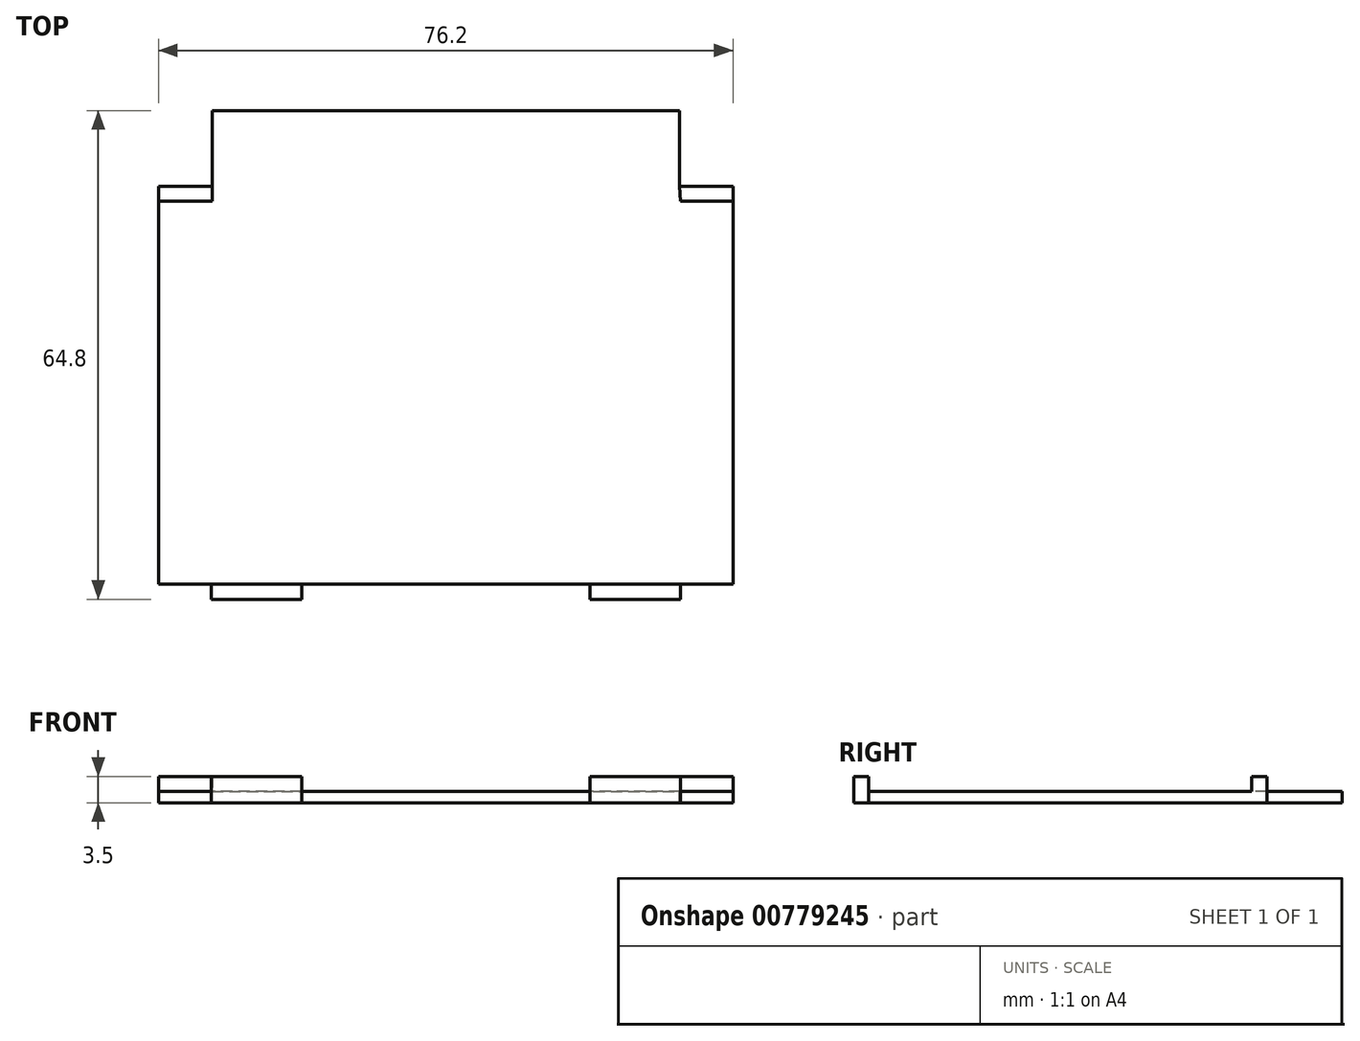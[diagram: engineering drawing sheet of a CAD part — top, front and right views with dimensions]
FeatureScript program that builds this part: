
annotation { "Feature Type Name" : "Feature", "Feature Type Description" : "" }
export const myFeature = defineFeature(function(context is Context, id is Id, definition is map)
    precondition{}
    {
        {
            var Q0;
            Q0=qCreatedBy(makeId("Top.planeOp"),FACE);
            var sketch = newSketch(context, id + "F0", { "sketchPlane" : qUnion([Q0])});
            skLineSegment(sketch, "E0.bottom", {"start": v(38.1, -25.4) * mm, "end": v(-38.1, -25.4) * mm});
            skLineSegment(sketch, "E0.top", {"start": v(38.1, 25.4) * mm, "end": v(-38.1, 25.4) * mm});
            skLineSegment(sketch, "E0.left", {"start": v(38.1, -25.4) * mm, "end": v(38.1, 25.4) * mm});
            skLineSegment(sketch, "E0.right", {"start": v(-38.1, -25.4) * mm, "end": v(-38.1, 25.4) * mm});
            skPoint(sketch, "E0.middle", {"position": v(0, 0) * mm});
            skLineSegment(sketch, "E1", {"start": v(-36.6, 25.4) * mm, "end": v(-36.6, -25.4) * mm});
            skLineSegment(sketch, "E2", {"start": v(-38.1, 25.4) * mm, "end": v(-38.1, 27.4) * mm});
            skLineSegment(sketch, "E3", {"start": v(-38.1, 27.4) * mm, "end": v(-31, 27.4) * mm});
            skLineSegment(sketch, "E4", {"start": v(-31.1, -25.4) * mm, "end": v(-31.1, -27.4) * mm});
            skLineSegment(sketch, "E5", {"start": v(-31.1, -27.4) * mm, "end": v(-19.1, -27.4) * mm});
            skLineSegment(sketch, "E6", {"start": v(-19.1, -27.4) * mm, "end": v(-19.1, -25.4) * mm});
            skLineSegment(sketch, "E7", {"start": v(0, 25.4) * mm, "end": v(0, -25.4) * mm, "construction": true});
            skLineSegment(sketch, "E8.MirrorCS", {"start": v(19.1, -27.4) * mm, "end": v(19.1, -25.4) * mm});
            skLineSegment(sketch, "E9.MirrorCS", {"start": v(31.1, -27.4) * mm, "end": v(19.1, -27.4) * mm});
            skLineSegment(sketch, "E10.MirrorCS", {"start": v(31.1, -25.4) * mm, "end": v(31.1, -27.4) * mm});
            skLineSegment(sketch, "E11.MirrorCS", {"start": v(36.6, 25.4) * mm, "end": v(36.6, -25.4) * mm});
            skLineSegment(sketch, "E12.MirrorCS", {"start": v(38.1, 25.4) * mm, "end": v(38.1, 27.4) * mm});
            skLineSegment(sketch, "E13.MirrorCS", {"start": v(38.1, 27.4) * mm, "end": v(31, 27.4) * mm});
            skLineSegment(sketch, "E14.MirrorCS", {"start": v(31, 27.4) * mm, "end": v(31.1, 25.4) * mm});
            skLineSegment(sketch, "E15.bottom", {"start": v(-31, 37.4) * mm, "end": v(31, 37.4) * mm});
            skLineSegment(sketch, "E15.left", {"start": v(-31, 37.4) * mm, "end": v(-31, 25.4) * mm});
            skLineSegment(sketch, "E15.right", {"start": v(31, 37.4) * mm, "end": v(31, 25.4) * mm});
            skLineSegment(sketch, "E16", {"start": v(0, 25.4) * mm, "end": v(0, 37.4) * mm});
            skSolve(sketch);
        }
        {
            var Q0;
            Q0 = qSketchRegion(id + "F0", true);
            extrude(context, id + "F1", {"entities" : qUnion([Q0]), "oppositeDirection" : true, "depth" : 1.5 * mm, "offsetDistance" : 25 * mm});
        }
        {
            var Q0;
            {var subQ1=sQuery(id+"F0.wireOp",EDGE,"E2");Q0=makeQuery(id+"F0.imprint","IMPRINT",FACE,{"disambiguationData":[TD([[makeQuery(id+"F0.imprint","IMPRINT",EDGE,{"derivedFrom":subQ1}),-1.0]])]});}
            var Q1;
            {var subQ0=sQuery(id+"F0.wireOp",EDGE,"E12.MirrorCS");Q1=makeQuery(id+"F0.imprint","IMPRINT",FACE,{"disambiguationData":[TD([[makeQuery(id+"F0.imprint","IMPRINT",EDGE,{"derivedFrom":subQ0}),1.0]])]});}
            var Q2;
            {var subQ0=sQuery(id+"F0.wireOp",EDGE,"E8.MirrorCS");Q2=makeQuery(id+"F0.imprint","IMPRINT",FACE,{"disambiguationData":[TD([[makeQuery(id+"F0.imprint","IMPRINT",EDGE,{"derivedFrom":subQ0}),-1.0]])]});}
            var Q3;
            {var subQ0=sQuery(id+"F0.wireOp",EDGE,"E4");Q3=makeQuery(id+"F0.imprint","IMPRINT",FACE,{"disambiguationData":[TD([[makeQuery(id+"F0.imprint","IMPRINT",EDGE,{"derivedFrom":subQ0}),1.0]])]});}
            extrude(context, id + "F2", {"entities" : qUnion([Q0, Q1, Q2, Q3]), "operationType" : NewBodyOperationType.ADD, "depth" : 2 * mm, "offsetDistance" : 25 * mm});
        }
    });
